FCSTD DOCUMENT  (FreeCAD 1.0R39285 (Git))
Label: Shelves
License: All rights reserved
LicenseURL: https://en.wikipedia.org/wiki/All_rights_reserved
objects: Sketcher::SketchObject×3, PartDesign::Body×1
note: 7 computed .brp shape members not serialized (recipe doc carries the construction recipe); baked Part::Feature solids carry a one-line shape summary decoded from their .brp

FEATURE [Sketcher::SketchObject] Sketch  label="Shelf_0"
  ArcFitTolerance = 1e-06
  AttachmentSupport = -> [XY_Plane]
  FullyConstrained = true
  MakeInternals = false
  MapMode = 5
  sketch-geometry (65):
    g0: LineSegment StartX=0 StartY=247.5 StartZ=0 EndX=-287 EndY=247.5 EndZ=0
    g1: LineSegment StartX=-290 StartY=244.5 StartZ=0 EndX=-290 EndY=220.5 EndZ=0
    g2: LineSegment StartX=-293 StartY=217.5 StartZ=0 EndX=-317 EndY=217.5 EndZ=0
    g3: LineSegment StartX=-320 StartY=214.5 StartZ=0 EndX=-320 EndY=190.5 EndZ=0
    g4: LineSegment StartX=-323 StartY=187.5 StartZ=0 EndX=-347 EndY=187.5 EndZ=0
    g5: LineSegment StartX=-350 StartY=184.5 StartZ=0 EndX=-350 EndY=0 EndZ=0
    g6: ArcOfCircle CenterX=-287 CenterY=244.5 CenterZ=0 NormalX=0 NormalY=0 NormalZ=1 AngleXU=0 Radius=3 StartAngle=1.5708 EndAngle=3.14159
    g7: GeomPoint [constr] X=-290 Y=247.5 Z=0
    g8: ArcOfCircle CenterX=-293 CenterY=220.5 CenterZ=0 NormalX=0 NormalY=0 NormalZ=1 AngleXU=0 Radius=3 StartAngle=4.71239 EndAngle=6.28319
    g9: GeomPoint [constr] X=-290 Y=217.5 Z=0
    g10: ArcOfCircle CenterX=-317 CenterY=214.5 CenterZ=0 NormalX=0 NormalY=0 NormalZ=1 AngleXU=0 Radius=3 StartAngle=1.5708 EndAngle=3.14159
    g11: GeomPoint [constr] X=-320 Y=217.5 Z=0
    g12: ArcOfCircle CenterX=-323 CenterY=190.5 CenterZ=0 NormalX=0 NormalY=0 NormalZ=1 AngleXU=0 Radius=3 StartAngle=4.71239 EndAngle=6.28319
    g13: GeomPoint [constr] X=-320 Y=187.5 Z=0
    g14: ArcOfCircle CenterX=-347 CenterY=184.5 CenterZ=0 NormalX=0 NormalY=0 NormalZ=1 AngleXU=0 Radius=3 StartAngle=1.5708 EndAngle=3.14159
    g15: GeomPoint [constr] X=-350 Y=187.5 Z=0
    g16: LineSegment StartX=0 StartY=247.5 StartZ=0 EndX=316 EndY=247.5 EndZ=0
    g17: LineSegment StartX=350 StartY=213.5 StartZ=0 EndX=350 EndY=0 EndZ=0
    g18: LineSegment StartX=0 StartY=-247.5 StartZ=0 EndX=-287 EndY=-247.5 EndZ=0
    g19: LineSegment StartX=-290 StartY=-244.5 StartZ=0 EndX=-290 EndY=-220.5 EndZ=0
    g20: LineSegment StartX=-293 StartY=-217.5 StartZ=0 EndX=-317 EndY=-217.5 EndZ=0
    g21: LineSegment StartX=-320 StartY=-214.5 StartZ=0 EndX=-320 EndY=-190.5 EndZ=0
    g22: LineSegment StartX=-323 StartY=-187.5 StartZ=0 EndX=-347 EndY=-187.5 EndZ=0
    g23: LineSegment StartX=-350 StartY=-184.5 StartZ=0 EndX=-350 EndY=0 EndZ=0
    g24: ArcOfCircle CenterX=-287 CenterY=-244.5 CenterZ=0 NormalX=0 NormalY=0 NormalZ=1 AngleXU=0 Radius=3 StartAngle=3.14159 EndAngle=4.71239
    g25: GeomPoint [constr] X=-290 Y=-247.5 Z=0
    g26: ArcOfCircle CenterX=-293 CenterY=-220.5 CenterZ=0 NormalX=0 NormalY=0 NormalZ=1 AngleXU=0 Radius=3 StartAngle=-3.6e-15 EndAngle=1.5708
    g27: GeomPoint [constr] X=-290 Y=-217.5 Z=0
    g28: ArcOfCircle CenterX=-317 CenterY=-214.5 CenterZ=0 NormalX=0 NormalY=0 NormalZ=1 AngleXU=0 Radius=3 StartAngle=3.14159 EndAngle=4.71239
    g29: GeomPoint [constr] X=-320 Y=-217.5 Z=0
    g30: ArcOfCircle CenterX=-323 CenterY=-190.5 CenterZ=0 NormalX=0 NormalY=0 NormalZ=1 AngleXU=0 Radius=3 StartAngle=4.4e-15 EndAngle=1.5708
    g31: GeomPoint [constr] X=-320 Y=-187.5 Z=0
    g32: ArcOfCircle CenterX=-347 CenterY=-184.5 CenterZ=0 NormalX=0 NormalY=0 NormalZ=1 AngleXU=0 Radius=3 StartAngle=3.14159 EndAngle=4.71239
    g33: GeomPoint [constr] X=-350 Y=-187.5 Z=0
    g34: LineSegment StartX=0 StartY=-247.5 StartZ=0 EndX=316 EndY=-247.5 EndZ=0
    g35: LineSegment StartX=350 StartY=-213.5 StartZ=0 EndX=350 EndY=0 EndZ=0
    g36: Circle CenterX=270 CenterY=167.5 CenterZ=0 NormalX=0 NormalY=0 NormalZ=1 AngleXU=0 Radius=30
    g37: ArcOfCircle CenterX=-338 CenterY=0 CenterZ=0 NormalX=0 NormalY=0 NormalZ=1 AngleXU=0 Radius=2.5 StartAngle=1.5708 EndAngle=4.71239
    g38: ArcOfCircle CenterX=-332 CenterY=-2e-16 CenterZ=0 NormalX=0 NormalY=0 NormalZ=1 AngleXU=0 Radius=2.5 StartAngle=4.71239 EndAngle=7.85398
    g39: LineSegment StartX=-338 StartY=2.5 StartZ=0 EndX=-332 EndY=2.5 EndZ=0
    g40: LineSegment StartX=-338 StartY=-2.5 StartZ=0 EndX=-332 EndY=-2.5 EndZ=0
    g41: GeomPoint [constr] X=-335 Y=-1e-16 Z=0
    g42: GeomPoint [constr] X=-335 Y=187.5 Z=0
    g43: LineSegment [constr] StartX=-335 StartY=-1e-16 StartZ=0 EndX=-335 EndY=187.5 EndZ=0
    g44: ArcOfCircle CenterX=338 CenterY=2e-16 CenterZ=0 NormalX=0 NormalY=0 NormalZ=1 AngleXU=0 Radius=2.5 StartAngle=4.71239 EndAngle=7.85398
    g45: ArcOfCircle CenterX=332 CenterY=1e-16 CenterZ=0 NormalX=0 NormalY=0 NormalZ=1 AngleXU=0 Radius=2.5 StartAngle=1.5708 EndAngle=4.71239
    g46: LineSegment StartX=338 StartY=2.5 StartZ=0 EndX=332 EndY=2.5 EndZ=0
    g47: LineSegment StartX=338 StartY=-2.5 StartZ=0 EndX=332 EndY=-2.5 EndZ=0
    g48: GeomPoint [constr] X=335 Y=-1e-16 Z=0
    g49: LineSegment StartX=319 StartY=244.5 StartZ=0 EndX=319 EndY=219.5 EndZ=0
    g50: LineSegment StartX=347 StartY=216.5 StartZ=0 EndX=322 EndY=216.5 EndZ=0
    g51: LineSegment StartX=319 StartY=-244.5 StartZ=0 EndX=319 EndY=-219.5 EndZ=0
    g52: LineSegment StartX=347 StartY=-216.5 StartZ=0 EndX=322 EndY=-216.5 EndZ=0
    g53: ArcOfCircle CenterX=316 CenterY=244.5 CenterZ=0 NormalX=0 NormalY=0 NormalZ=1 AngleXU=0 Radius=3 StartAngle=3.9e-15 EndAngle=1.5708
    g54: GeomPoint [constr] X=319 Y=247.5 Z=0
    g55: ArcOfCircle CenterX=322 CenterY=219.5 CenterZ=0 NormalX=0 NormalY=0 NormalZ=1 AngleXU=0 Radius=3 StartAngle=3.14159 EndAngle=4.71239
    g56: GeomPoint [constr] X=319 Y=216.5 Z=0
    g57: ArcOfCircle CenterX=347 CenterY=213.5 CenterZ=0 NormalX=0 NormalY=0 NormalZ=1 AngleXU=0 Radius=3 StartAngle=4.4e-15 EndAngle=1.5708
    g58: GeomPoint [constr] X=350 Y=216.5 Z=0
    g59: ArcOfCircle CenterX=347 CenterY=-213.5 CenterZ=0 NormalX=0 NormalY=0 NormalZ=1 AngleXU=0 Radius=3 StartAngle=4.71239 EndAngle=6.28319
    g60: GeomPoint [constr] X=350 Y=-216.5 Z=0
    g61: ArcOfCircle CenterX=322 CenterY=-219.5 CenterZ=0 NormalX=0 NormalY=0 NormalZ=1 AngleXU=0 Radius=3 StartAngle=1.5708 EndAngle=3.14159
    g62: GeomPoint [constr] X=319 Y=-216.5 Z=0
    g63: ArcOfCircle CenterX=316 CenterY=-244.5 CenterZ=0 NormalX=0 NormalY=0 NormalZ=1 AngleXU=0 Radius=3 StartAngle=4.71239 EndAngle=6.28319
    g64: GeomPoint [constr] X=319 Y=-247.5 Z=0
  constraints (143):
    c: PointOnObject(g0,g-2)
    c: Horizontal(g0)
    c: Horizontal(g2)
    c: Vertical(g3)
    c: PointOnObject(g5,g-1)
    c: Vertical(g5)
    c: Vertical(g1)
    c: Horizontal(g4)
    c: Distance(g-2,g5) = 350
    c: Distance(g13,g15) = 30
    c: Distance(g-1,g0) = 247.5
    c: PointOnObject(g7,g0)
    c: PointOnObject(g7,g1)
    c: Tangent(g0,g6) = -1.5708
    c: Tangent(g1,g6) = -1.5708
    c: PointOnObject(g9,g1)
    c: PointOnObject(g9,g2)
    c: Tangent(g1,g8) = 1.5708
    c: Tangent(g2,g8) = 1.5708
    c: PointOnObject(g11,g2)
    c: PointOnObject(g11,g3)
    c: Tangent(g2,g10) = -1.5708
    c: Tangent(g3,g10) = -1.5708
    c: PointOnObject(g13,g3)
    c: PointOnObject(g13,g4)
    c: Tangent(g3,g12) = 1.5708
    c: Tangent(g4,g12) = 1.5708
    c: PointOnObject(g15,g4)
    c: PointOnObject(g15,g5)
    c: Tangent(g4,g14) = -1.5708
    c: Tangent(g5,g14) = -1.5708
    c: Radius(g6) = 3
    c: Equal(g8,g6)
    c: Equal(g8,g10)
    c: Equal(g12,g10)
    c: Equal(g12,g14)
    c: Distance(g1,g3) = 30
    c: Distance(g2,g0) = 30
    c: Distance(g2,g4) = 30
    c: Symmetric(g5,g17,g-2)
    c: Coincident(g0,g16)
    c: Symmetric(g0,g18,g-1)
    c: Symmetric(g0,g18,g-1)
    c: Symmetric(g1,g19,g-1)
    c: Symmetric(g1,g19,g-1)
    c: Symmetric(g2,g20,g-1)
    c: Symmetric(g2,g20,g-1)
    c: Symmetric(g3,g21,g-1)
    c: Symmetric(g3,g21,g-1)
    c: Symmetric(g4,g22,g-1)
    c: Symmetric(g4,g22,g-1)
    c: Symmetric(g5,g23,g-1)
    c: Equal(g6,g24)
    c: Symmetric(g6,g24,g-1)
    c: Symmetric(g6,g24,g-1)
    c: Symmetric(g7,g25,g-1)
    c: Equal(g8,g26)
    c: Symmetric(g8,g26,g-1)
    c: Symmetric(g8,g26,g-1)
    c: Symmetric(g9,g27,g-1)
    c: Equal(g10,g28)
    c: Symmetric(g10,g28,g-1)
    c: Symmetric(g10,g28,g-1)
    c: Symmetric(g11,g29,g-1)
    c: Equal(g12,g30)
    c: Symmetric(g12,g30,g-1)
    c: Symmetric(g12,g30,g-1)
    c: Symmetric(g13,g31,g-1)
    c: Equal(g14,g32)
    c: Symmetric(g14,g32,g-1)
    c: Symmetric(g14,g32,g-1)
    c: Symmetric(g15,g33,g-1)
    c: Symmetric(g16,g34,g-1)
    c: Symmetric(g54,g64,g-1)
    c: Symmetric(g58,g60,g-1)
    c: Coincident(g17,g35)
    c: Coincident(g5,g23)
    c: Distance(g36,g17) = 80
    c: Distance(g36,g16) = 80
    c: Diameter(g36) = 60
    c: Tangent(g37,g39) = 1.5708
    c: Tangent(g37,g40) = -1.5708
    c: Tangent(g38,g39) = 1.5708
    c: Tangent(g38,g40) = -1.5708
    c: Equal(g37,g38)
    c: Horizontal(g40)
    c: Radius(g37) = 2.5
    c: PointOnObject(g37,g-1)
    c: DistanceX(g39,g39) = 6
    c: Symmetric(g37,g38,g41)
    c: Symmetric(g4,g4,g42)
    c: Coincident(g43,g41)
    c: Coincident(g43,g42)
    c: Vertical(g43)
    c: Symmetric(g37,g44,g-2)
    c: Symmetric(g37,g44,g-2)
    c: Symmetric(g38,g45,g-2)
    c: Symmetric(g38,g45,g-2)
    c: Symmetric(g39,g46,g-2)
    c: Symmetric(g39,g46,g-2)
    c: Symmetric(g40,g47,g-2)
    c: Symmetric(g40,g47,g-2)
    c: Symmetric(g41,g48,g-2)
    c: Tangent(g45,g46)
    c: Tangent(g46,g44)
    c: Horizontal(g50)
    c: Vertical(g49)
    c: Distance(g58,g56) = 31
    c: Horizontal(g52)
    c: Vertical(g51)
    c: DistanceY(g56,g54) = 31
    c: Horizontal(g16)
    c: PointOnObject(g54,g16)
    c: PointOnObject(g54,g49)
    c: Tangent(g16,g53) = 1.5708
    c: Tangent(g49,g53) = 1.5708
    c: PointOnObject(g56,g49)
    c: PointOnObject(g56,g50)
    c: Tangent(g49,g55) = -1.5708
    c: Tangent(g50,g55) = 1.5708
    c: PointOnObject(g58,g50)
    c: PointOnObject(g58,g17)
    c: Tangent(g50,g57) = -1.5708
    c: Tangent(g17,g57) = 1.5708
    c: PointOnObject(g60,g35)
    c: PointOnObject(g60,g52)
    c: Tangent(g35,g59) = -1.5708
    c: Tangent(g52,g59) = 1.5708
    c: PointOnObject(g62,g52)
    c: PointOnObject(g62,g51)
    c: Tangent(g52,g61) = -1.5708
    c: Tangent(g51,g61) = 1.5708
    c: PointOnObject(g64,g51)
    c: PointOnObject(g64,g34)
    c: Tangent(g51,g63) = -1.5708
    c: Tangent(g34,g63) = -1.5708
    c: Equal(g57,g55)
    c: Equal(g55,g53)
    c: Equal(g57,g59)
    c: Equal(g59,g61)
    c: Equal(g61,g63)
    c: Equal(g63,g24)
    c: Vertical(g17)
FEATURE [Sketcher::SketchObject] Sketch001  label="Shelf_1"
  ArcFitTolerance = 1e-06
  AttachmentSupport = -> [XY_Plane]
  ExternalGeometry = -> [Sketch]
  FullyConstrained = true
  MakeInternals = false
  MapMode = 5
  sketch-geometry (62):
    g0: LineSegment StartX=-350 StartY=213.5 StartZ=0 EndX=-350 EndY=-213.5 EndZ=0
    g1: LineSegment StartX=-316 StartY=-247.5 StartZ=0 EndX=316 EndY=-247.5 EndZ=0
    g2: LineSegment StartX=350 StartY=-213.5 StartZ=0 EndX=350 EndY=213.5 EndZ=0
    g3: LineSegment StartX=316 StartY=247.5 StartZ=0 EndX=-316 EndY=247.5 EndZ=0
    g4: LineSegment StartX=-347 StartY=216.5 StartZ=0 EndX=-322 EndY=216.5 EndZ=0
    g5: LineSegment StartX=-319 StartY=219.5 StartZ=0 EndX=-319 EndY=244.5 EndZ=0
    g6: LineSegment StartX=319 StartY=244.5 StartZ=0 EndX=319 EndY=219.5 EndZ=0
    g7: LineSegment StartX=322 StartY=216.5 StartZ=0 EndX=347 EndY=216.5 EndZ=0
    g8: LineSegment StartX=347 StartY=-216.5 StartZ=0 EndX=322 EndY=-216.5 EndZ=0
    g9: LineSegment StartX=319 StartY=-219.5 StartZ=0 EndX=319 EndY=-244.5 EndZ=0
    g10: LineSegment StartX=-319 StartY=-244.5 StartZ=0 EndX=-319 EndY=-219.5 EndZ=0
    g11: LineSegment StartX=-322 StartY=-216.5 StartZ=0 EndX=-347 EndY=-216.5 EndZ=0
    g12: ArcOfCircle CenterX=-316 CenterY=244.5 CenterZ=0 NormalX=0 NormalY=0 NormalZ=1 AngleXU=0 Radius=3 StartAngle=1.5708 EndAngle=3.14159
    g13: GeomPoint [constr] X=-319 Y=247.5 Z=0
    g14: ArcOfCircle CenterX=-322 CenterY=219.5 CenterZ=0 NormalX=0 NormalY=0 NormalZ=1 AngleXU=0 Radius=3 StartAngle=4.71239 EndAngle=6.28319
    g15: GeomPoint [constr] X=-319 Y=216.5 Z=0
    g16: ArcOfCircle CenterX=-347 CenterY=213.5 CenterZ=0 NormalX=0 NormalY=0 NormalZ=1 AngleXU=0 Radius=3 StartAngle=1.5708 EndAngle=3.14159
    g17: GeomPoint [constr] X=-350 Y=216.5 Z=0
    g18: ArcOfCircle CenterX=-347 CenterY=-213.5 CenterZ=0 NormalX=0 NormalY=0 NormalZ=1 AngleXU=0 Radius=3 StartAngle=3.14159 EndAngle=4.71239
    g19: GeomPoint [constr] X=-350 Y=-216.5 Z=0
    g20: ArcOfCircle CenterX=-322 CenterY=-219.5 CenterZ=0 NormalX=0 NormalY=0 NormalZ=1 AngleXU=0 Radius=3 StartAngle=1e-15 EndAngle=1.5708
    g21: GeomPoint [constr] X=-319 Y=-216.5 Z=0
    g22: ArcOfCircle CenterX=-316 CenterY=-244.5 CenterZ=0 NormalX=0 NormalY=0 NormalZ=1 AngleXU=0 Radius=3 StartAngle=3.14159 EndAngle=4.71239
    g23: GeomPoint [constr] X=-319 Y=-247.5 Z=0
    g24: ArcOfCircle CenterX=316 CenterY=-244.5 CenterZ=0 NormalX=0 NormalY=0 NormalZ=1 AngleXU=0 Radius=3 StartAngle=4.71239 EndAngle=6.28319
    g25: ArcOfCircle CenterX=322 CenterY=-219.5 CenterZ=0 NormalX=0 NormalY=0 NormalZ=1 AngleXU=0 Radius=3 StartAngle=1.5708 EndAngle=3.14159
    g26: GeomPoint [constr] X=319 Y=-216.5 Z=0
    g27: ArcOfCircle CenterX=347 CenterY=-213.5 CenterZ=0 NormalX=0 NormalY=0 NormalZ=1 AngleXU=0 Radius=3 StartAngle=4.71239 EndAngle=6.28319
    g28: GeomPoint [constr] X=350 Y=-216.5 Z=0
    g29: ArcOfCircle CenterX=347 CenterY=213.5 CenterZ=0 NormalX=0 NormalY=0 NormalZ=1 AngleXU=0 Radius=3 StartAngle=1.2e-15 EndAngle=1.5708
    g30: GeomPoint [constr] X=350 Y=216.5 Z=0
    g31: ArcOfCircle CenterX=322 CenterY=219.5 CenterZ=0 NormalX=0 NormalY=0 NormalZ=1 AngleXU=0 Radius=3 StartAngle=3.14159 EndAngle=4.71239
    g32: GeomPoint [constr] X=319 Y=216.5 Z=0
    g33: ArcOfCircle CenterX=316 CenterY=244.5 CenterZ=0 NormalX=0 NormalY=0 NormalZ=1 AngleXU=0 Radius=3 StartAngle=2.1e-15 EndAngle=1.5708
    g34: GeomPoint [constr] X=319 Y=247.5 Z=0
    g35: Circle CenterX=270 CenterY=167.5 CenterZ=0 NormalX=0 NormalY=0 NormalZ=1 AngleXU=0 Radius=20
    g36: ArcOfCircle CenterX=-337.5 CenterY=201.5 CenterZ=0 NormalX=0 NormalY=0 NormalZ=1 AngleXU=0 Radius=3 StartAngle=1.5708 EndAngle=4.71239
    g37: ArcOfCircle CenterX=-331.5 CenterY=201.5 CenterZ=0 NormalX=0 NormalY=0 NormalZ=1 AngleXU=0 Radius=3 StartAngle=4.71239 EndAngle=7.85398
    g38: LineSegment StartX=-337.5 StartY=204.5 StartZ=0 EndX=-331.5 EndY=204.5 EndZ=0
    g39: LineSegment StartX=-337.5 StartY=198.5 StartZ=0 EndX=-331.5 EndY=198.5 EndZ=0
    g40: LineSegment [constr] StartX=-337.5 StartY=201.5 StartZ=0 EndX=-331.5 EndY=201.5 EndZ=0
    g41: GeomPoint [constr] X=-334.5 Y=201.5 Z=0
    g42: GeomPoint [constr] X=-334.5 Y=216.5 Z=0
    g43: LineSegment [constr] StartX=-334.5 StartY=216.5 StartZ=0 EndX=-334.5 EndY=201.5 EndZ=0
    g44: ArcOfCircle CenterX=-337.5 CenterY=-201.5 CenterZ=0 NormalX=0 NormalY=0 NormalZ=1 AngleXU=0 Radius=3 StartAngle=1.5708 EndAngle=4.71239
    g45: ArcOfCircle CenterX=-331.5 CenterY=-201.5 CenterZ=0 NormalX=0 NormalY=0 NormalZ=1 AngleXU=0 Radius=3 StartAngle=4.71239 EndAngle=7.85398
    g46: LineSegment StartX=-337.5 StartY=-204.5 StartZ=0 EndX=-331.5 EndY=-204.5 EndZ=0
    g47: LineSegment StartX=-337.5 StartY=-198.5 StartZ=0 EndX=-331.5 EndY=-198.5 EndZ=0
    g48: LineSegment [constr] StartX=-337.5 StartY=-201.5 StartZ=0 EndX=-331.5 EndY=-201.5 EndZ=0
    g49: GeomPoint [constr] X=-334.5 Y=-201.5 Z=0
    g50: ArcOfCircle CenterX=337.5 CenterY=-201.5 CenterZ=0 NormalX=0 NormalY=0 NormalZ=1 AngleXU=0 Radius=3 StartAngle=4.71239 EndAngle=7.85398
    g51: ArcOfCircle CenterX=331.5 CenterY=-201.5 CenterZ=0 NormalX=0 NormalY=0 NormalZ=1 AngleXU=0 Radius=3 StartAngle=1.5708 EndAngle=4.71239
    g52: LineSegment StartX=337.5 StartY=-204.5 StartZ=0 EndX=331.5 EndY=-204.5 EndZ=0
    g53: LineSegment StartX=337.5 StartY=-198.5 StartZ=0 EndX=331.5 EndY=-198.5 EndZ=0
    g54: LineSegment [constr] StartX=337.5 StartY=-201.5 StartZ=0 EndX=331.5 EndY=-201.5 EndZ=0
    g55: GeomPoint [constr] X=334.5 Y=-201.5 Z=0
    g56: ArcOfCircle CenterX=337.5 CenterY=201.5 CenterZ=0 NormalX=0 NormalY=0 NormalZ=1 AngleXU=0 Radius=3 StartAngle=4.71239 EndAngle=7.85398
    g57: ArcOfCircle CenterX=331.5 CenterY=201.5 CenterZ=0 NormalX=0 NormalY=0 NormalZ=1 AngleXU=0 Radius=3 StartAngle=1.5708 EndAngle=4.71239
    g58: LineSegment StartX=337.5 StartY=204.5 StartZ=0 EndX=331.5 EndY=204.5 EndZ=0
    g59: LineSegment StartX=337.5 StartY=198.5 StartZ=0 EndX=331.5 EndY=198.5 EndZ=0
    g60: LineSegment [constr] StartX=337.5 StartY=201.5 StartZ=0 EndX=331.5 EndY=201.5 EndZ=0
    g61: GeomPoint [constr] X=334.5 Y=201.5 Z=0
  constraints (134):
    c: Vertical(g0)
    c: Vertical(g2)
    c: Horizontal(g1)
    c: Horizontal(g3)
    c: Vertical(g5)
    c: Horizontal(g4)
    c: Horizontal(g7)
    c: Vertical(g6)
    c: Vertical(g9)
    c: Horizontal(g8)
    c: Horizontal(g11)
    c: Vertical(g10)
    c: PointOnObject(g30,g-4)
    c: PointOnObject(g23,g-6)
    c: PointOnObject(g17,g-3)
    c: Symmetric(g15,g32,g-2)
    c: Symmetric(g15,g21,g-1)
    c: Symmetric(g32,g26,g-1)
    c: PointOnObject(g13,g-5)
    c: DistanceX(g17,g15) = 31
    c: Distance(g15,g13) = 31
    c: PointOnObject(g13,g3)
    c: PointOnObject(g13,g5)
    c: Tangent(g3,g12) = -1.5708
    c: Tangent(g5,g12) = 1.5708
    c: PointOnObject(g15,g5)
    c: PointOnObject(g15,g4)
    c: Tangent(g5,g14) = -1.5708
    c: Tangent(g4,g14) = -1.5708
    c: PointOnObject(g17,g4)
    c: PointOnObject(g17,g0)
    c: Tangent(g4,g16) = 1.5708
    c: Tangent(g0,g16) = -1.5708
    c: PointOnObject(g19,g0)
    c: PointOnObject(g19,g11)
    c: Tangent(g0,g18) = -1.5708
    c: Tangent(g11,g18) = 1.5708
    c: PointOnObject(g21,g11)
    c: PointOnObject(g21,g10)
    c: Tangent(g11,g20) = -1.5708
    c: Tangent(g10,g20) = -1.5708
    c: PointOnObject(g23,g10)
    c: PointOnObject(g23,g1)
    c: Tangent(g10,g22) = 1.5708
    c: Tangent(g1,g22) = -1.5708
    c: Tangent(g1,g24) = -1.5708
    c: Tangent(g9,g24) = 1.5708
    c: PointOnObject(g26,g9)
    c: PointOnObject(g26,g8)
    c: Tangent(g9,g25) = -1.5708
    c: Tangent(g8,g25) = -1.5708
    c: PointOnObject(g28,g8)
    c: PointOnObject(g28,g2)
    c: Tangent(g8,g27) = 1.5708
    c: Tangent(g2,g27) = -1.5708
    c: PointOnObject(g30,g2)
    c: PointOnObject(g30,g7)
    c: Tangent(g2,g29) = -1.5708
    c: Tangent(g7,g29) = 1.5708
    c: PointOnObject(g32,g7)
    c: PointOnObject(g32,g6)
    c: Tangent(g7,g31) = -1.5708
    c: Tangent(g6,g31) = -1.5708
    c: PointOnObject(g34,g6)
    c: PointOnObject(g34,g3)
    c: Tangent(g6,g33) = 1.5708
    c: Tangent(g3,g33) = -1.5708
    c: Equal(g14,g12)
    c: Equal(g12,g16)
    c: Radius(g12) = 3
    c: Equal(g12,g33)
    c: Equal(g33,g31)
    c: Equal(g31,g29)
    c: Equal(g29,g27)
    c: Equal(g27,g25)
    c: Equal(g25,g24)
    c: Equal(g24,g22)
    c: Equal(g22,g20)
    c: Equal(g20,g18)
    c: Coincident(g35,g-7)
    c: Diameter(g35) = 40
    c: Tangent(g36,g38) = 1.5708
    c: Tangent(g36,g39) = -1.5708
    c: Tangent(g37,g38) = 1.5708
    c: Tangent(g37,g39) = -1.5708
    c: Equal(g36,g37)
    c: Coincident(g40,g36)
    c: Coincident(g40,g37)
    c: Symmetric(g40,g40,g41)
    c: Symmetric(g4,g4,g42)
    c: Coincident(g43,g42)
    c: Coincident(g43,g41)
    c: Vertical(g43)
    c: DistanceX(g38,g38) = 6
    c: Radius(g36) = 3
    c: Symmetric(g36,g44,g-1)
    c: Symmetric(g36,g44,g-1)
    c: Symmetric(g37,g45,g-1)
    c: Symmetric(g37,g45,g-1)
    c: Symmetric(g38,g46,g-1)
    c: Symmetric(g38,g46,g-1)
    c: Symmetric(g39,g47,g-1)
    c: Symmetric(g39,g47,g-1)
    c: Symmetric(g40,g48,g-1)
    c: Symmetric(g40,g48,g-1)
    c: Symmetric(g41,g49,g-1)
    c: Coincident(g44,g48)
    c: Coincident(g48,g45)
    c: Equal(g36,g56)
    c: Symmetric(g36,g56,g-2)
    c: Symmetric(g36,g56,g-2)
    c: Equal(g37,g57)
    c: Symmetric(g37,g57,g-2)
    c: Symmetric(g37,g57,g-2)
    c: Symmetric(g38,g58,g-2)
    c: Symmetric(g38,g58,g-2)
    c: Symmetric(g39,g59,g-2)
    c: Symmetric(g39,g59,g-2)
    c: Symmetric(g40,g60,g-2)
    c: Symmetric(g40,g60,g-2)
    c: Symmetric(g41,g61,g-2)
    c: Equal(g44,g50)
    c: Symmetric(g44,g50,g-2)
    c: Symmetric(g44,g50,g-2)
    c: Equal(g45,g51)
    c: Symmetric(g45,g51,g-2)
    c: Symmetric(g45,g51,g-2)
    c: Symmetric(g46,g52,g-2)
    c: Symmetric(g46,g52,g-2)
    c: Symmetric(g47,g53,g-2)
    c: Symmetric(g47,g53,g-2)
    c: Symmetric(g48,g54,g-2)
    c: Symmetric(g48,g54,g-2)
    c: Symmetric(g49,g55,g-2)
FEATURE [Sketcher::SketchObject] Sketch002  label="RackTop"
  ArcFitTolerance = 1e-06
  AttachmentSupport = -> [XY_Plane]
  ExternalGeometry = -> [Sketch]
  FullyConstrained = true
  MakeInternals = false
  MapMode = 5
  sketch-geometry (24):
    g0: LineSegment StartX=-350 StartY=243.5 StartZ=0 EndX=-350 EndY=-243.5 EndZ=0
    g1: LineSegment StartX=-346 StartY=-247.5 StartZ=0 EndX=346 EndY=-247.5 EndZ=0
    g2: LineSegment StartX=350 StartY=-243.5 StartZ=0 EndX=350 EndY=243.5 EndZ=0
    g3: LineSegment StartX=346 StartY=247.5 StartZ=0 EndX=-346 EndY=247.5 EndZ=0
    g4: ArcOfCircle CenterX=-346 CenterY=243.5 CenterZ=0 NormalX=0 NormalY=0 NormalZ=1 AngleXU=0 Radius=4 StartAngle=1.5708 EndAngle=3.14159
    g5: GeomPoint [constr] X=-350 Y=247.5 Z=0
    g6: ArcOfCircle CenterX=346 CenterY=243.5 CenterZ=0 NormalX=0 NormalY=0 NormalZ=1 AngleXU=0 Radius=4 StartAngle=-9e-16 EndAngle=1.5708
    g7: GeomPoint [constr] X=350 Y=247.5 Z=0
    g8: ArcOfCircle CenterX=346 CenterY=-243.5 CenterZ=0 NormalX=0 NormalY=0 NormalZ=1 AngleXU=0 Radius=4 StartAngle=4.71239 EndAngle=6.28319
    g9: GeomPoint [constr] X=350 Y=-247.5 Z=0
    g10: ArcOfCircle CenterX=-346 CenterY=-243.5 CenterZ=0 NormalX=0 NormalY=0 NormalZ=1 AngleXU=0 Radius=4 StartAngle=3.14159 EndAngle=4.71239
    g11: GeomPoint [constr] X=-350 Y=-247.5 Z=0
    g12: ArcOfCircle CenterX=-338 CenterY=0 CenterZ=0 NormalX=0 NormalY=0 NormalZ=1 AngleXU=0 Radius=2.5 StartAngle=1.5708 EndAngle=4.71239
    g13: ArcOfCircle CenterX=-332 CenterY=-1e-16 CenterZ=0 NormalX=0 NormalY=0 NormalZ=1 AngleXU=0 Radius=2.5 StartAngle=4.71239 EndAngle=7.85398
    g14: LineSegment StartX=-338 StartY=2.5 StartZ=0 EndX=-332 EndY=2.5 EndZ=0
    g15: LineSegment StartX=-338 StartY=-2.5 StartZ=0 EndX=-332 EndY=-2.5 EndZ=0
    g16: ArcOfCircle CenterX=332 CenterY=1e-16 CenterZ=0 NormalX=0 NormalY=0 NormalZ=1 AngleXU=0 Radius=2.5 StartAngle=1.5708 EndAngle=4.71239
    g17: ArcOfCircle CenterX=338 CenterY=2e-16 CenterZ=0 NormalX=0 NormalY=0 NormalZ=1 AngleXU=0 Radius=2.5 StartAngle=4.71239 EndAngle=7.85398
    g18: LineSegment StartX=332 StartY=2.5 StartZ=0 EndX=338 EndY=2.5 EndZ=0
    g19: LineSegment StartX=332 StartY=-2.5 StartZ=0 EndX=338 EndY=-2.5 EndZ=0
    g20: Circle CenterX=-150 CenterY=-150 CenterZ=0 NormalX=0 NormalY=0 NormalZ=1 AngleXU=0 Radius=7.5
    g21: Circle CenterX=0 CenterY=-150 CenterZ=0 NormalX=0 NormalY=0 NormalZ=1 AngleXU=0 Radius=7.5
    g22: Circle CenterX=150 CenterY=-150 CenterZ=0 NormalX=0 NormalY=0 NormalZ=1 AngleXU=0 Radius=7.5
    g23: LineSegment [constr] StartX=-150 StartY=-150 StartZ=0 EndX=150 EndY=-150 EndZ=0
  constraints (54):
    c: Vertical(g0)
    c: Vertical(g2)
    c: Horizontal(g1)
    c: Horizontal(g3)
    c: PointOnObject(g-5,g3)
    c: PointOnObject(g-4,g0)
    c: PointOnObject(g-3,g2)
    c: PointOnObject(g-6,g1)
    c: PointOnObject(g5,g3)
    c: PointOnObject(g5,g0)
    c: Tangent(g3,g4) = -1.5708
    c: Tangent(g0,g4) = -1.5708
    c: PointOnObject(g7,g3)
    c: PointOnObject(g7,g2)
    c: Tangent(g3,g6) = -1.5708
    c: Tangent(g2,g6) = -1.5708
    c: PointOnObject(g9,g2)
    c: PointOnObject(g9,g1)
    c: Tangent(g2,g8) = -1.5708
    c: Tangent(g1,g8) = -1.5708
    c: PointOnObject(g11,g0)
    c: PointOnObject(g11,g1)
    c: Tangent(g0,g10) = -1.5708
    c: Tangent(g1,g10) = -1.5708
    c: Equal(g10,g8)
    c: Equal(g8,g6)
    c: Equal(g6,g4)
    c: Radius(g4) = 4
    c: Tangent(g12,g14) = 1.5708
    c: Tangent(g12,g15) = -1.5708
    c: Tangent(g13,g14) = 1.5708
    c: Tangent(g13,g15) = -1.5708
    c: Equal(g12,g13)
    c: Coincident(g12,g-7)
    c: Coincident(g13,g-8)
    c: Equal(g12,g-7)
    c: Tangent(g16,g18) = 1.5708
    c: Tangent(g16,g19) = -1.5708
    c: Tangent(g17,g18) = 1.5708
    c: Tangent(g17,g19) = -1.5708
    c: Equal(g16,g17)
    c: Coincident(g16,g-11)
    c: Coincident(g17,g-12)
    c: Equal(g16,g-11)
    c: PointOnObject(g21,g-2)
    c: Coincident(g23,g20)
    c: Coincident(g23,g22)
    c: Horizontal(g23)
    c: Equal(g22,g21)
    c: Equal(g21,g20)
    c: Diameter(g20) = 15
    c: Symmetric(g20,g22,g21)
    c: DistanceX(g23,g23) = 300
    c: Distance(g-1,g23) = 150
FEATURE [PartDesign::Body] Body  label="Foobar"
  AllowCompound = false
  Group = -> [Sketch,Sketch001,Sketch002]
  Origin = -> Origin
